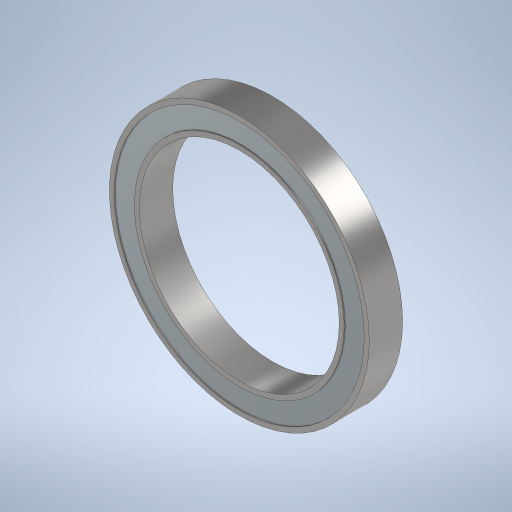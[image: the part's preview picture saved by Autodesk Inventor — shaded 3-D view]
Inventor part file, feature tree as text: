
AUTODESK INVENTOR PART (.ipt)
format: ipt  version: 2024 (Build 280153000, 153)  size: 284,672 bytes
history: native  units: mm
features: extrude x2, sketch x1
ambient origin geometry x8: Origin, YZ Plane, XZ Plane, XY Plane, X Axis, Y Axis, Z Axis, Center Point
bodies: Solid1 (feature_tree)
feature tree (3):
  sketch  "Sketch1"  dims[d0=60.0mm d1=78.0mm d2=1.5mm d3=1.5mm d4=10.0mm d5=0.0mm d6=9.5mm d7=0.0mm]
  extrude  "Extrusion1"  Depth=9.5mm
  extrude  "Extrusion2"  Depth=9.5mm
